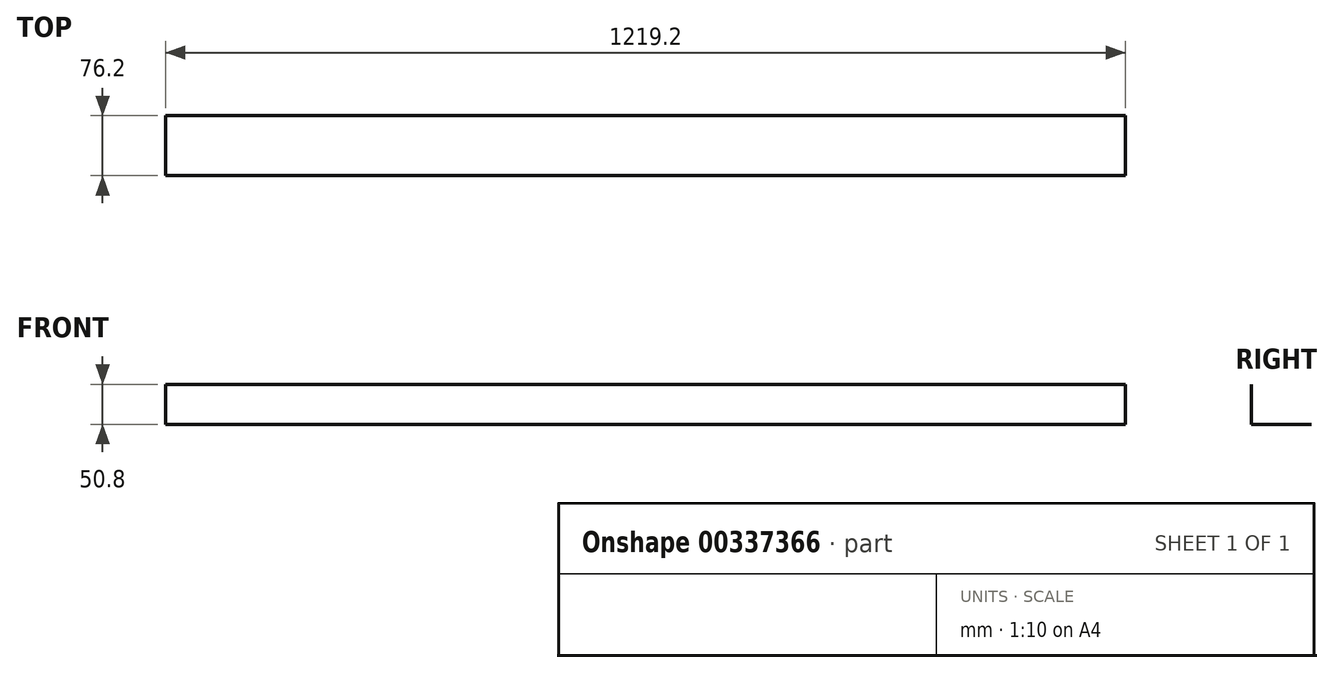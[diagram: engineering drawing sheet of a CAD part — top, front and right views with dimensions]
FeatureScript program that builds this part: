
annotation { "Feature Type Name" : "Feature", "Feature Type Description" : "" }
export const myFeature = defineFeature(function(context is Context, id is Id, definition is map)
    precondition{}
    {
        {
            var Q0;
            Q0=qCreatedBy(makeId("Right.planeOp"),FACE);
            var sketch = newSketch(context, id + "F0", { "sketchPlane" : qUnion([Q0])});
            skLineSegment(sketch, "E0", {"start": v(-79.16, 5.34) * mm, "end": v(-79.16, -45.46) * mm});
            skLineSegment(sketch, "E1", {"start": v(-79.16, -45.46) * mm, "end": v(-2.96, -45.46) * mm});
            skSolve(sketch);
        }
        {
            var Q0;
            Q0 = qSketchRegion(id + "F0", true);
            var Q1;
            Q1=sQuery(id+"F0.wireOp",EDGE,"E0");
            var Q2;
            Q2=sQuery(id+"F0.wireOp",EDGE,"E1");
            extrude(context, id + "F1", {"entities" : qUnion([Q0]), "bodyType" : ToolBodyType.SURFACE, "surfaceEntities" : qUnion([Q1, Q2]), "depth" : 1219.2 * mm});
        }
    });
